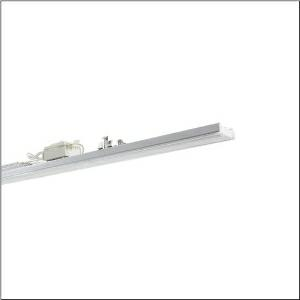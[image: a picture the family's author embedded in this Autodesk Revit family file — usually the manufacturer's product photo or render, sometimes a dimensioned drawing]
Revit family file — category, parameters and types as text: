
# Revit family: licross_r__11_recessed_mo_51te10dn495g_4ea1
name_source: partatom
category: Lighting Fixtures
units: mm (PartAtom-declared; Revit-internal decimal feet)

## family parameters
Cut with Voids When Loaded = No
Host = Face
Light Source = No
Part Type = Normal
Room Calculation Point = No
Round Connector Dimension = Use Diameter
Shared = No

## types (1)
- --- (1 x LED, 9960 lm, 56.7 W, 4000K)
    Apparent Load = 57 VA
    CIE Flux Codes = 50 81 96 100 100
    Color Rendering = 80
    Color Temperature = 4000K
    Default Elevation = 1800 mm
    Description = Licross® 11 Recessed MO, luminaire insert, of sheet steel, galvanised, coil coated, white, length: 1.500mm, width: 66mm, height: 67mm, LED rated luminous flux: 9.960lm, light colour: 840, control gear: DALI 2, with plug, 5-pole, with phase selection, mains connection: 220..240V, AC, 50/60Hz, rated input power: 57W, halogen-free wiring, primary optical cover: cover, of PMMA, light emission: direct distribution, primary light characteristic: symmetric, protection rating (complete): IP54, insulation class (complete): insulation class I (protective earthing), certification: CE, ENEC, VDE, UKCA, protection symbol: D if used in an environment with non-conductive dust loads with corresponding accessories, impact resistance: IK06, permissible ambient temperature for indoor applications: -25..+35°C, corresponds to IFS (International Featured Standards) requirements for safety and quality in the food industry, reducing of maximum allowable ambient temperature of 5°C with ceiling mounting, LABS conformity tested according to VDMA 24364:2018-05, packaging unit: 1 piece
    Height = 58 mm
    Lamp = 1 x LED
    Lamp Light Flux = 9960 lm
    Lamp Power = 56.7 W
    Lamp count = 1
    Length = 1500 mm
    Luminous efficacy = 176 lm/W
    Manufacturer = Siteco
    ModVariant = No
    Model = 51TE10DN495G
    Mounting Place = Ceiling
    Mounting Type = Pendant
    Number of Poles = 1
    OnlyDefault = Yes
    Power Factor = 1
    Product Name = Licross® 11 Recessed MO
    Product group = luminaire insert
    ProductGroupID = 902
    Protection Class = Protection class I
    Protection Degree = IP 54
    RLX_Detail_Level = 1
    RLX_Emergency_Light_Flux = 0 lm
    RLX_Emergency_Type = 0
    RLX_Emergency_Type_DB = No
    RlxData = <blob elided: 24329 chars, md5=85a11994>
    Socket = socket
    Standby Power = 0 W
    System Light Flux = 9960 lm
    System Power = 57 W
    Type Comments = factory setting: luminous flux: 100 % | dim-lin: 254 | 378 mA
    Type Image = l_1296930.jpg
    URL = http://relux.com
    VarID = @adj_099858
    Voltage = 0 V
    Weight = 0.00 kg
    Width = 66 mm

## geometry (parser evidence)
native form markers: Blend x4, Sweep x10
no freeform markers — native parametric forms only
